# Revit family: Haworth_Cappellini_Fronzoni64_Table_AP_PRELIMINARY
name_source: partatom
category: Furniture
revit_build: Autodesk Revit 2018 (Build: 20170223_1515(x64)
units: mm (PartAtom-declared; Revit-internal decimal feet)

## family parameters
Always vertical = Yes
Cut with Voids When Loaded = No
OmniClass Number = 23.40.70.14.64.21
OmniClass Title = Systems Furniture
Room Calculation Point = No
Shared = No
Work Plane-Based = No

## types (3) — shared parameters
Actual Depth = 1000 mm  [stored 3.28084 ft]
Assembly Code = E2020200
Chamfer = 2 mm  [stored 0.00656168 ft]
Description = Haworth - Cappellini - Fronzoni 64 - Table
Glide Height = 3 mm  [stored 0.00984252 ft]
Glide Offset = 10 mm  [stored 0.0328084 ft]
Leg Thickness = 20 mm  [stored 0.0656168 ft]
Manufacturer = Haworth
Model = FR_2X
Revision Number = 4
Size = Verify Final Dim. w/ Haworth
Table Top Thickness = 26 mm
URL = https://www.haworth.com
URL - Product = https://www.haworth.com
Warranty = http://www.haworth.com

## per-type parameters (varying)
| type | Actual Height | Actual Width |
| High Rectangle | 700 mm  [stored 2.29659 ft] | 2000 mm  [stored 6.56168 ft] |
| High Square | 700 mm  [stored 2.29659 ft] | 1000 mm  [stored 3.28084 ft] |
| Low Square | 300 mm | 1000 mm  [stored 3.28084 ft] |

type visibility flags: 3 boolean params named "<type name>" — each type sets only its own to Yes (folded from table)

note: [stored X ft] marks values corroborated as IEEE doubles in the binary element streams (Revit-internal decimal feet)

## geometry (parser evidence)
native form markers: Sweep x2
no freeform markers — native parametric forms only
